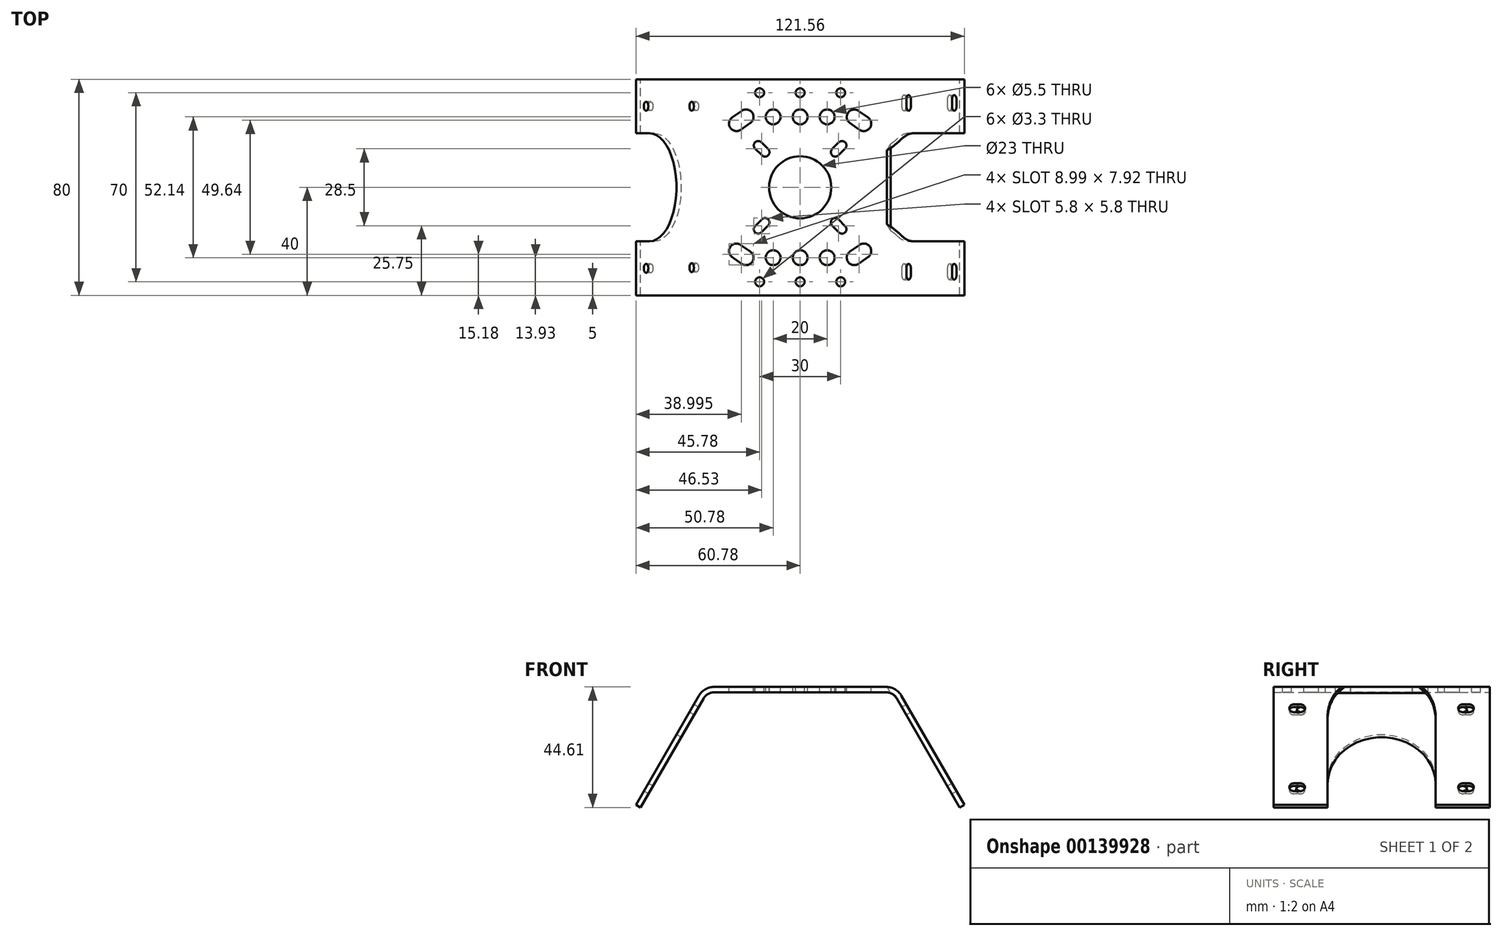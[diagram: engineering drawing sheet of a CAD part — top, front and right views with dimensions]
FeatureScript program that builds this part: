
annotation { "Feature Type Name" : "Feature", "Feature Type Description" : "" }
export const myFeature = defineFeature(function(context is Context, id is Id, definition is map)
    precondition{}
    {
        {
            var Q0;
            Q0=qCreatedBy(makeId("Front.planeOp"),FACE);
            var sketch = newSketch(context, id + "F0", { "sketchPlane" : qUnion([Q0])});
            skLineSegment(sketch, "E0", {"start": v(-31.85, 0) * mm, "end": v(31.85, 0) * mm});
            skLineSegment(sketch, "E1", {"start": v(-35.75, -2.25) * mm, "end": v(-59.05, -42.6) * mm});
            skLineSegment(sketch, "E2", {"start": v(35.75, -2.25) * mm, "end": v(59.05, -42.6) * mm});
            skPoint(sketch, "E3.visualSharp", {"position": v(-34.45, 0) * mm});
            skArc(sketch, "E3.filletArc", {"start": v(-31.85, 0) * mm, "mid": v(-34.1, -0.6) * mm, "end": v(-35.75, -2.25) * mm});
            skPoint(sketch, "E4.visualSharp", {"position": v(34.45, 0) * mm});
            skArc(sketch, "E4.filletArc", {"start": v(35.75, -2.25) * mm, "mid": v(34.1, -0.6) * mm, "end": v(31.85, 0) * mm});
            skLineSegment(sketch, "E5.0", {"start": v(37.48, -1.25) * mm, "end": v(60.78, -41.6) * mm});
            skLineSegment(sketch, "E5.1", {"start": v(-37.48, -1.25) * mm, "end": v(-60.78, -41.6) * mm});
            skArc(sketch, "E5.2", {"start": v(-31.85, 2) * mm, "mid": v(-35.1, 1.13) * mm, "end": v(-37.48, -1.25) * mm});
            skLineSegment(sketch, "E5.3", {"start": v(-31.85, 2) * mm, "end": v(31.85, 2) * mm});
            skArc(sketch, "E5.4", {"start": v(37.48, -1.25) * mm, "mid": v(35.1, 1.13) * mm, "end": v(31.85, 2) * mm});
            skLineSegment(sketch, "E6", {"start": v(-60.78, -41.6) * mm, "end": v(-59.05, -42.6) * mm});
            skLineSegment(sketch, "E7", {"start": v(60.78, -41.6) * mm, "end": v(59.05, -42.6) * mm});
            skSolve(sketch);
        }
        {
            var Q0;
            Q0 = qSketchRegion(id + "F0", true);
            var Q1;
            Q1 = qConstructionFilter(qBodyType(qCreatedBy(id + "F0" ,EDGE), BodyType.WIRE), ConstructionObject.NO);
            extrude(context, id + "F1", {"entities" : qUnion([Q0]), "surfaceEntities" : qUnion([Q1]), "depth" : 80 * mm});
        }
        {
            var Q0;
            Q0=makeQuery(id+"F1.opExtrude","SWEPT_FACE",FACE,{"disambiguationData":[OSD([sQuery(id+"F0.wireOp",EDGE,"E5.0")])]});
            var sketch = newSketch(context, id + "F2", { "sketchPlane" : qUnion([Q0])});
            skArc(sketch, "E8", {"start": v(-20, -28.88) * mm, "mid": v(-40, -8.88) * mm, "end": v(-60, -28.88) * mm});
            skLineSegment(sketch, "E9", {"start": v(-20, -28.88) * mm, "end": v(-20, -66.42) * mm});
            skLineSegment(sketch, "E10", {"start": v(-60, -28.88) * mm, "end": v(-60, -66.42) * mm});
            skLineSegment(sketch, "E11", {"start": v(-20, -66.42) * mm, "end": v(0, -66.42) * mm});
            skLineSegment(sketch, "E12", {"start": v(0, -66.42) * mm, "end": v(0, -19.82) * mm});
            skLineSegment(sketch, "E13", {"start": v(-20, -66.42) * mm, "end": v(-60, -66.42) * mm});
            skArc(sketch, "E14", {"start": v(-70, -60.57) * mm, "mid": v(-68.35, -58.92) * mm, "end": v(-70, -57.27) * mm});
            skArc(sketch, "E15", {"start": v(-72.5, -57.27) * mm, "mid": v(-74.15, -58.92) * mm, "end": v(-72.5, -60.57) * mm});
            skArc(sketch, "E16", {"start": v(-72.5, -23.52) * mm, "mid": v(-74.15, -25.17) * mm, "end": v(-72.5, -26.82) * mm});
            skArc(sketch, "E17", {"start": v(-70, -26.82) * mm, "mid": v(-68.35, -25.17) * mm, "end": v(-70, -23.52) * mm});
            skArc(sketch, "E18", {"start": v(-7.5, -26.82) * mm, "mid": v(-5.85, -25.17) * mm, "end": v(-7.5, -23.52) * mm});
            skArc(sketch, "E19", {"start": v(-10, -23.52) * mm, "mid": v(-11.65, -25.17) * mm, "end": v(-10, -26.82) * mm});
            skArc(sketch, "E20", {"start": v(-7.5, -60.57) * mm, "mid": v(-5.85, -58.92) * mm, "end": v(-7.5, -57.27) * mm});
            skArc(sketch, "E21", {"start": v(-10, -57.27) * mm, "mid": v(-11.65, -58.92) * mm, "end": v(-10, -60.57) * mm});
            skLineSegment(sketch, "E22", {"start": v(-7.5, -23.52) * mm, "end": v(-10, -23.52) * mm});
            skLineSegment(sketch, "E23", {"start": v(-7.5, -26.82) * mm, "end": v(-10, -26.82) * mm});
            skLineSegment(sketch, "E24", {"start": v(-7.5, -57.27) * mm, "end": v(-10, -57.27) * mm});
            skLineSegment(sketch, "E25", {"start": v(-7.5, -60.57) * mm, "end": v(-10, -60.57) * mm});
            skLineSegment(sketch, "E26", {"start": v(-70, -23.52) * mm, "end": v(-72.5, -23.52) * mm});
            skLineSegment(sketch, "E27", {"start": v(-70, -26.82) * mm, "end": v(-72.5, -26.82) * mm});
            skLineSegment(sketch, "E28", {"start": v(-70, -57.27) * mm, "end": v(-72.5, -57.27) * mm});
            skLineSegment(sketch, "E29", {"start": v(-70, -60.57) * mm, "end": v(-72.5, -60.57) * mm});
            skSolve(sketch);
        }
        {
            var Q0;
            Q0 = qSketchRegion(id + "F2", true);
            extrude(context, id + "F3", {"entities" : qUnion([Q0]), "operationType" : NewBodyOperationType.REMOVE, "oppositeDirection" : true, "depth" : 3 * mm});
        }
        {
            var Q0;
            Q0=makeQuery(id+"F1.opExtrude","SWEPT_FACE",FACE,{"disambiguationData":[OSD([sQuery(id+"F0.wireOp",EDGE,"E5.1")])]});
            var sketch = newSketch(context, id + "F4", { "sketchPlane" : qUnion([Q0])});
            skCircle(sketch, "E30", {"center": v(40, -56.42) * mm, "radius": 20 * mm});
            skCircle(sketch, "E31", {"center": v(70, -58.92) * mm, "radius": 1.65 * mm});
            skCircle(sketch, "E32", {"center": v(69.75, -25.17) * mm, "radius": 1.65 * mm});
            skCircle(sketch, "E33", {"center": v(10, -58.92) * mm, "radius": 1.65 * mm});
            skCircle(sketch, "E34", {"center": v(10, -25.17) * mm, "radius": 1.65 * mm});
            skLineSegment(sketch, "E35.bottom", {"start": v(20, -56.42) * mm, "end": v(60, -56.42) * mm});
            skLineSegment(sketch, "E35.top", {"start": v(20, -66.42) * mm, "end": v(60, -66.42) * mm});
            skLineSegment(sketch, "E35.left", {"start": v(20, -56.42) * mm, "end": v(20, -66.42) * mm});
            skLineSegment(sketch, "E35.right", {"start": v(60, -56.42) * mm, "end": v(60, -66.42) * mm});
            skSolve(sketch);
        }
        {
            var Q0;
            Q0 = qSketchRegion(id + "F4", true);
            extrude(context, id + "F5", {"entities" : qUnion([Q0]), "operationType" : NewBodyOperationType.REMOVE, "oppositeDirection" : true, "depth" : 3 * mm});
        }
        {
            var Q0;
            Q0=makeQuery(id+"F1.opExtrude","SWEPT_FACE",FACE,{"disambiguationData":[OSD([sQuery(id+"F0.wireOp",EDGE,"E5.3")])]});
            var sketch = newSketch(context, id + "F6", { "sketchPlane" : qUnion([Q0])});
            skCircle(sketch, "E36", {"center": v(0, -40) * mm, "radius": 11.5 * mm});
            skCircle(sketch, "E37", {"center": v(-15, -5) * mm, "radius": 1.65 * mm});
            skCircle(sketch, "E38", {"center": v(0, -5) * mm, "radius": 1.65 * mm});
            skCircle(sketch, "E39", {"center": v(15, -5) * mm, "radius": 1.65 * mm});
            skCircle(sketch, "E40", {"center": v(-10, -13.93) * mm, "radius": 2.75 * mm});
            skCircle(sketch, "E41", {"center": v(0, -13.93) * mm, "radius": 2.75 * mm});
            skCircle(sketch, "E42", {"center": v(10, -13.93) * mm, "radius": 2.75 * mm});
            skCircle(sketch, "E43", {"center": v(-10, -66.07) * mm, "radius": 2.75 * mm});
            skCircle(sketch, "E44", {"center": v(0, -66.07) * mm, "radius": 2.75 * mm});
            skCircle(sketch, "E45", {"center": v(10, -66.07) * mm, "radius": 2.75 * mm});
            skCircle(sketch, "E46", {"center": v(0, -75) * mm, "radius": 1.65 * mm});
            skCircle(sketch, "E47", {"center": v(-15, -75) * mm, "radius": 1.65 * mm});
            skCircle(sketch, "E48", {"center": v(15, -75) * mm, "radius": 1.65 * mm});
            skLineSegment(sketch, "E49", {"start": v(-22, -61.32) * mm, "end": v(-18.42, -63.82) * mm});
            skLineSegment(sketch, "E50", {"start": v(-21.58, -68.32) * mm, "end": v(-25.15, -65.82) * mm});
            skLineSegment(sketch, "E51", {"start": v(-25.15, -14.18) * mm, "end": v(-21.58, -11.68) * mm});
            skLineSegment(sketch, "E52", {"start": v(-18.42, -16.18) * mm, "end": v(-22, -18.68) * mm});
            skLineSegment(sketch, "E53", {"start": v(21.58, -11.68) * mm, "end": v(25.15, -14.18) * mm});
            skLineSegment(sketch, "E54", {"start": v(18.42, -16.18) * mm, "end": v(22, -18.68) * mm});
            skLineSegment(sketch, "E55", {"start": v(18.42, -63.82) * mm, "end": v(22, -61.32) * mm});
            skLineSegment(sketch, "E56", {"start": v(25.15, -65.82) * mm, "end": v(21.58, -68.32) * mm});
            skArc(sketch, "E57", {"start": v(-14.33, -23.33) * mm, "mid": v(-16.67, -23.33) * mm, "end": v(-16.67, -25.67) * mm});
            skArc(sketch, "E58", {"start": v(-14.17, -28.17) * mm, "mid": v(-11.83, -28.17) * mm, "end": v(-11.83, -25.83) * mm});
            skArc(sketch, "E59", {"start": v(-11.83, -54.17) * mm, "mid": v(-11.83, -51.83) * mm, "end": v(-14.17, -51.83) * mm});
            skArc(sketch, "E60", {"start": v(-16.67, -54.33) * mm, "mid": v(-16.67, -56.67) * mm, "end": v(-14.33, -56.67) * mm});
            skArc(sketch, "E61", {"start": v(14.17, -51.83) * mm, "mid": v(11.83, -51.83) * mm, "end": v(11.83, -54.17) * mm});
            skArc(sketch, "E62", {"start": v(14.33, -56.67) * mm, "mid": v(16.67, -56.67) * mm, "end": v(16.67, -54.33) * mm});
            skArc(sketch, "E63", {"start": v(11.83, -25.83) * mm, "mid": v(11.83, -28.17) * mm, "end": v(14.17, -28.17) * mm});
            skArc(sketch, "E64", {"start": v(16.67, -25.67) * mm, "mid": v(16.67, -23.33) * mm, "end": v(14.33, -23.33) * mm});
            skLineSegment(sketch, "E65", {"start": v(-16.67, -25.67) * mm, "end": v(-14.17, -28.17) * mm});
            skLineSegment(sketch, "E66", {"start": v(-14.33, -23.33) * mm, "end": v(-11.83, -25.83) * mm});
            skLineSegment(sketch, "E67", {"start": v(-14.17, -51.83) * mm, "end": v(-16.67, -54.33) * mm});
            skLineSegment(sketch, "E68", {"start": v(-14.33, -56.67) * mm, "end": v(-11.83, -54.17) * mm});
            skLineSegment(sketch, "E69", {"start": v(11.83, -54.17) * mm, "end": v(14.33, -56.67) * mm});
            skLineSegment(sketch, "E70", {"start": v(16.67, -54.33) * mm, "end": v(14.17, -51.83) * mm});
            skLineSegment(sketch, "E71", {"start": v(11.83, -25.83) * mm, "end": v(14.33, -23.33) * mm});
            skLineSegment(sketch, "E72", {"start": v(14.17, -28.17) * mm, "end": v(16.67, -25.67) * mm});
            skArc(sketch, "E73", {"start": v(18.42, -63.82) * mm, "mid": v(17.75, -67.65) * mm, "end": v(21.58, -68.32) * mm});
            skArc(sketch, "E74", {"start": v(25.15, -65.82) * mm, "mid": v(25.82, -62) * mm, "end": v(22, -61.32) * mm});
            skArc(sketch, "E75", {"start": v(-22, -61.32) * mm, "mid": v(-25.82, -62) * mm, "end": v(-25.15, -65.82) * mm});
            skArc(sketch, "E76", {"start": v(-21.58, -68.32) * mm, "mid": v(-17.75, -67.65) * mm, "end": v(-18.42, -63.82) * mm});
            skArc(sketch, "E77", {"start": v(-18.42, -16.18) * mm, "mid": v(-17.75, -12.35) * mm, "end": v(-21.58, -11.68) * mm});
            skArc(sketch, "E78", {"start": v(-25.15, -14.18) * mm, "mid": v(-25.82, -18) * mm, "end": v(-22, -18.68) * mm});
            skArc(sketch, "E79", {"start": v(21.58, -11.68) * mm, "mid": v(17.75, -12.35) * mm, "end": v(18.42, -16.18) * mm});
            skArc(sketch, "E80", {"start": v(22, -18.68) * mm, "mid": v(25.82, -18) * mm, "end": v(25.15, -14.18) * mm});
            skSolve(sketch);
        }
        {
            var Q0;
            Q0 = qSketchRegion(id + "F6", true);
            extrude(context, id + "F7", {"entities" : qUnion([Q0]), "operationType" : NewBodyOperationType.REMOVE, "oppositeDirection" : true, "depth" : 3 * mm});
        }
    });
